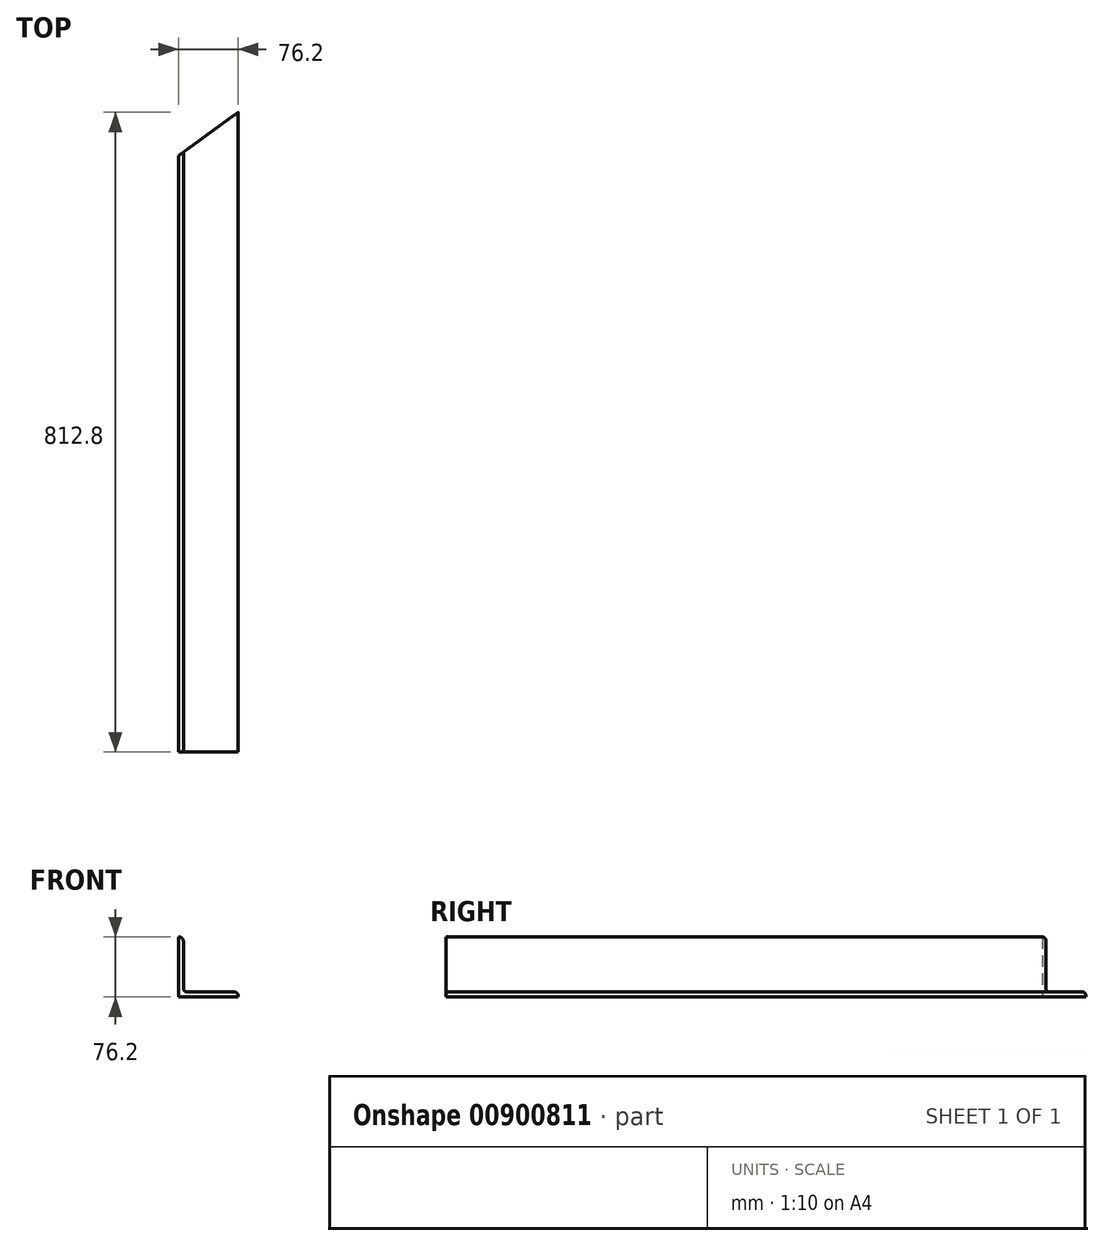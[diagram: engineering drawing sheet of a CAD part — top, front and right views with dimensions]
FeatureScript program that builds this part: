
annotation { "Feature Type Name" : "Feature", "Feature Type Description" : "" }
export const myFeature = defineFeature(function(context is Context, id is Id, definition is map)
    precondition{}
    {
        {
            var Q0;
            Q0=qCreatedBy(makeId("Front.planeOp"),FACE);
            var sketch = newSketch(context, id + "F0", { "sketchPlane" : qUnion([Q0])});
            skLineSegment(sketch, "E0.bottom", {"start": v(38.1, -38.1) * mm, "end": v(-38.1, -38.1) * mm});
            skLineSegment(sketch, "E0.top", {"start": v(-31.75, 38.1) * mm, "end": v(-38.1, 38.1) * mm});
            skLineSegment(sketch, "E0.left", {"start": v(38.1, -38.1) * mm, "end": v(38.1, -31.75) * mm});
            skLineSegment(sketch, "E0.right", {"start": v(-38.1, -38.1) * mm, "end": v(-38.1, 38.1) * mm});
            skPoint(sketch, "E0.middle", {"position": v(0, 0) * mm});
            skLineSegment(sketch, "E1.0", {"start": v(-31.75, -31.75) * mm, "end": v(-31.75, 38.1) * mm});
            skLineSegment(sketch, "E2.0", {"start": v(38.1, -31.75) * mm, "end": v(-31.75, -31.75) * mm});
            skPoint(sketch, "E3.orphan", {"position": v(38.1, 38.1) * mm});
            skSolve(sketch);
        }
        {
            var Q0;
            Q0 = qSketchRegion(id + "F0", true);
            extrude(context, id + "F1", {"entities" : qUnion([Q0]), "depth" : 812.8 * mm, "offsetDistance" : 25.4 * mm, "symmetric" : true});
        }
        {
            var Q0;
            Q0=makeQuery(id+"F1.opExtrude","SWEPT_EDGE",EDGE,{"disambiguationData":[OSD([sQuery(id+"F0.wireOp",EDGE,"E0.top"),sQuery(id+"F0.wireOp",EDGE,"E1.0")])]});
            var Q1;
            Q1=makeQuery(id+"F1.opExtrude","SWEPT_EDGE",EDGE,{"disambiguationData":[OSD([sQuery(id+"F0.wireOp",EDGE,"E0.left"),sQuery(id+"F0.wireOp",EDGE,"E2.0")])]});
            var Q2;
            Q2=makeQuery(id+"F1.opExtrude","SWEPT_EDGE",EDGE,{"disambiguationData":[OSD([sQuery(id+"F0.wireOp",EDGE,"E1.0"),sQuery(id+"F0.wireOp",EDGE,"E2.0")])]});
            fillet(context, id + "F2", {"entities" : qUnion([Q0, Q1, Q2]), "radius" : 5.08 * mm, "tangentPropagation" : true, "allowEdgeOverflow" : false});
        }
        {
            var Q0;
            Q0=makeQuery(id+"F1.opExtrude","SWEPT_FACE",FACE,{"disambiguationData":[OSD([sQuery(id+"F0.wireOp",EDGE,"E0.bottom")])]});
            var sketch = newSketch(context, id + "F3", { "sketchPlane" : qUnion([Q0])});
            skPoint(sketch, "E4.0", {"position": v(38.1, -406.4) * mm});
            skLineSegment(sketch, "E5", {"start": v(38.1, -406.4) * mm, "end": v(-38.1, -351.04) * mm});
            skLineSegment(sketch, "E6", {"start": v(-38.1, -351.04) * mm, "end": v(-38.1, -406.4) * mm});
            skLineSegment(sketch, "E7", {"start": v(-38.1, -406.4) * mm, "end": v(38.1, -406.4) * mm});
            skSolve(sketch);
        }
        {
            var Q0;
            Q0 = qSketchRegion(id + "F3", true);
            extrude(context, id + "F4", {"entities" : qUnion([Q0]), "operationType" : NewBodyOperationType.REMOVE, "oppositeDirection" : true, "depth" : 76.2 * mm, "offsetDistance" : 25.4 * mm});
        }
    });
